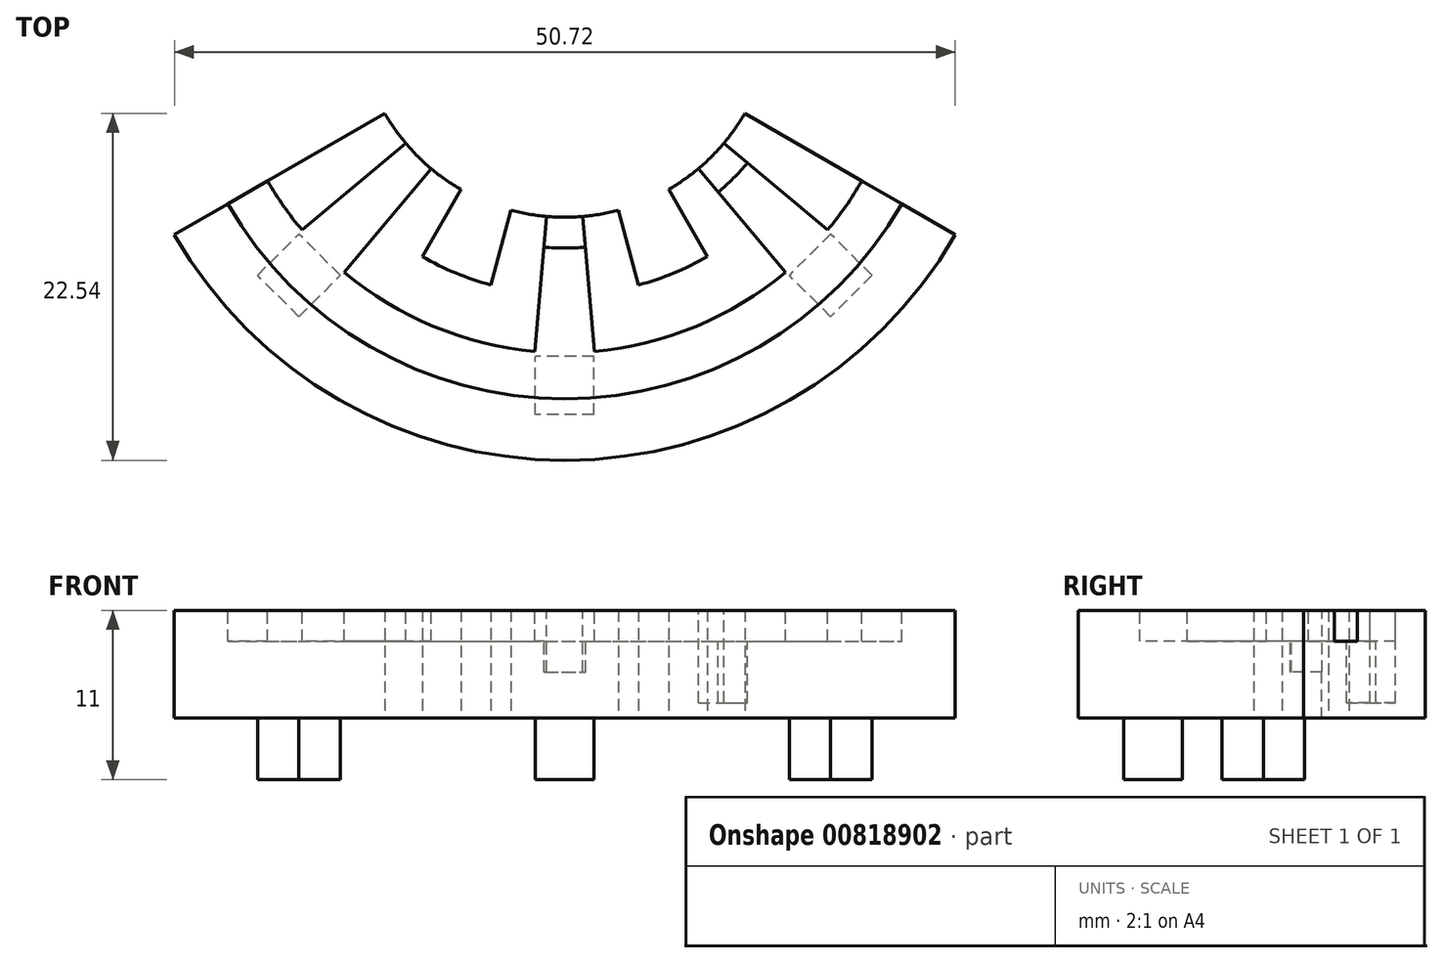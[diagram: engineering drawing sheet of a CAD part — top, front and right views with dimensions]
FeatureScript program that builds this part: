
annotation { "Feature Type Name" : "Feature", "Feature Type Description" : "" }
export const myFeature = defineFeature(function(context is Context, id is Id, definition is map)
    precondition{}
    {
        {
            var Q0;
            Q0=qCreatedBy(makeId("Top.planeOp"),FACE);
            var sketch = newSketch(context, id + "F0", { "sketchPlane" : qUnion([Q0])});
            skCircle(sketch, "E0", {"center": v(0, 0) * mm, "radius": 29.29 * mm});
            skCircle(sketch, "E1.4.0", {"center": v(0, -24.43) * mm, "radius": 1 * mm});
            skCircle(sketch, "E2", {"center": v(0, 0) * mm, "radius": 12.5 * mm});
            skLineSegment(sketch, "E3.bottom", {"start": v(1.9, -26.33) * mm, "end": v(-1.9, -26.33) * mm});
            skLineSegment(sketch, "E3.top", {"start": v(1.9, -22.53) * mm, "end": v(-1.9, -22.53) * mm});
            skLineSegment(sketch, "E3.left", {"start": v(1.9, -26.33) * mm, "end": v(1.9, -22.53) * mm});
            skLineSegment(sketch, "E3.right", {"start": v(-1.9, -26.33) * mm, "end": v(-1.9, -22.53) * mm});
            skLineSegment(sketch, "E4.1.0", {"start": v(19.96, -17.27) * mm, "end": v(17.27, -19.96) * mm});
            skLineSegment(sketch, "E4.1.1", {"start": v(19.96, -17.27) * mm, "end": v(17.27, -14.58) * mm});
            skLineSegment(sketch, "E4.1.2", {"start": v(17.27, -14.58) * mm, "end": v(14.58, -17.27) * mm});
            skLineSegment(sketch, "E4.1.3", {"start": v(17.27, -19.96) * mm, "end": v(14.58, -17.27) * mm});
            skLineSegment(sketch, "E4.2.0", {"start": v(26.33, 1.9) * mm, "end": v(26.33, -1.9) * mm});
            skLineSegment(sketch, "E4.2.1", {"start": v(26.33, 1.9) * mm, "end": v(22.53, 1.9) * mm});
            skLineSegment(sketch, "E4.2.2", {"start": v(22.53, 1.9) * mm, "end": v(22.53, -1.9) * mm});
            skLineSegment(sketch, "E4.2.3", {"start": v(26.33, -1.9) * mm, "end": v(22.53, -1.9) * mm});
            skLineSegment(sketch, "E4.3.0", {"start": v(17.27, 19.96) * mm, "end": v(19.96, 17.27) * mm});
            skLineSegment(sketch, "E4.3.1", {"start": v(17.27, 19.96) * mm, "end": v(14.58, 17.27) * mm});
            skLineSegment(sketch, "E4.3.2", {"start": v(14.58, 17.27) * mm, "end": v(17.27, 14.58) * mm});
            skLineSegment(sketch, "E4.3.3", {"start": v(19.96, 17.27) * mm, "end": v(17.27, 14.58) * mm});
            skLineSegment(sketch, "E4.4.0", {"start": v(-1.9, 26.33) * mm, "end": v(1.9, 26.33) * mm});
            skLineSegment(sketch, "E4.4.1", {"start": v(-1.9, 26.33) * mm, "end": v(-1.9, 22.53) * mm});
            skLineSegment(sketch, "E4.4.2", {"start": v(-1.9, 22.53) * mm, "end": v(1.9, 22.53) * mm});
            skLineSegment(sketch, "E4.4.3", {"start": v(1.9, 26.33) * mm, "end": v(1.9, 22.53) * mm});
            skLineSegment(sketch, "E4.5.0", {"start": v(-19.96, 17.27) * mm, "end": v(-17.27, 19.96) * mm});
            skLineSegment(sketch, "E4.5.1", {"start": v(-19.96, 17.27) * mm, "end": v(-17.27, 14.58) * mm});
            skLineSegment(sketch, "E4.5.2", {"start": v(-17.27, 14.58) * mm, "end": v(-14.58, 17.27) * mm});
            skLineSegment(sketch, "E4.5.3", {"start": v(-17.27, 19.96) * mm, "end": v(-14.58, 17.27) * mm});
            skLineSegment(sketch, "E4.6.0", {"start": v(-26.33, -1.9) * mm, "end": v(-26.33, 1.9) * mm});
            skLineSegment(sketch, "E4.6.1", {"start": v(-26.33, -1.9) * mm, "end": v(-22.53, -1.9) * mm});
            skLineSegment(sketch, "E4.6.2", {"start": v(-22.53, -1.9) * mm, "end": v(-22.53, 1.9) * mm});
            skLineSegment(sketch, "E4.6.3", {"start": v(-26.33, 1.9) * mm, "end": v(-22.53, 1.9) * mm});
            skLineSegment(sketch, "E4.7.0", {"start": v(-17.27, -19.96) * mm, "end": v(-19.96, -17.27) * mm});
            skLineSegment(sketch, "E4.7.1", {"start": v(-17.27, -19.96) * mm, "end": v(-14.58, -17.27) * mm});
            skLineSegment(sketch, "E4.7.2", {"start": v(-14.58, -17.27) * mm, "end": v(-17.27, -14.58) * mm});
            skLineSegment(sketch, "E4.7.3", {"start": v(-19.96, -17.27) * mm, "end": v(-17.27, -14.58) * mm});
            skLineSegment(sketch, "E5", {"start": v(0, 0) * mm, "end": v(25.36, -14.64) * mm});
            skLineSegment(sketch, "E6", {"start": v(0, 0) * mm, "end": v(-25.36, -14.64) * mm});
            skLineSegment(sketch, "E7", {"start": v(0, 0) * mm, "end": v(14.64, -25.36) * mm});
            skLineSegment(sketch, "E8", {"start": v(0, 0) * mm, "end": v(7.58, -28.29) * mm});
            skLineSegment(sketch, "E9", {"start": v(0, 0) * mm, "end": v(-7.58, -28.29) * mm});
            skLineSegment(sketch, "E10", {"start": v(0, 0) * mm, "end": v(-14.64, -25.36) * mm});
            skCircle(sketch, "E11", {"center": v(0, 0) * mm, "radius": 18.53 * mm});
            skCircle(sketch, "E12.0", {"center": v(0, 0) * mm, "radius": 13.5 * mm});
            skSolve(sketch);
        }
        {
            var Q0;
            Q0=makeQuery(id+"F0.imprint","IMPRINT",FACE,{"disambiguationData":[TD([[makeQuery(id+"F0.imprint","IMPRINT",EDGE,{"derivedFrom":sQuery(id+"F0.wireOp",EDGE,"E4.1.0")}),1.0]])]});
            var Q1;
            Q1=makeQuery(id+"F0.imprint","IMPRINT",FACE,{"disambiguationData":[TD([[makeQuery(id+"F0.imprint","IMPRINT",EDGE,{"derivedFrom":sQuery(id+"F0.wireOp",EDGE,"E4.1.0")}),-1.0]])]});
            var Q2;
            {var subQ0=sQuery(id+"F0.wireOp",EDGE,"E12.0");var subQ1=sQuery(id+"F0.wireOp",EDGE,"E5");var subQ2=makeQuery(id+"F0.imprint","INTERSECT",VERTEX,{"derivedFrom":[subQ1,subQ0]});Q2=makeQuery(id+"F0.imprint","IMPRINT",FACE,{"disambiguationData":[TD([[makeQuery(id+"F0.imprint","IMPRINT",EDGE,{"disambiguationData":[TD([[subQ2,-1.0]])],"derivedFrom":subQ1}),-1.0]])]});}
            var Q3;
            {var subQ0=sQuery(id+"F0.wireOp",EDGE,"E7");var subQ1=sQuery(id+"F0.wireOp",EDGE,"E0");var subQ2=makeQuery(id+"F0.imprint","INTERSECT",VERTEX,{"derivedFrom":[subQ1,subQ0]});Q3=makeQuery(id+"F0.imprint","IMPRINT",FACE,{"disambiguationData":[TD([[makeQuery(id+"F0.imprint","IMPRINT",EDGE,{"disambiguationData":[TD([[subQ2,1.0]])],"derivedFrom":subQ1}),1.0]])]});}
            var Q4;
            Q4=makeQuery(id+"F0.imprint","IMPRINT",FACE,{"disambiguationData":[TD([[makeQuery(id+"F0.imprint","IMPRINT",EDGE,{"derivedFrom":sQuery(id+"F0.wireOp",EDGE,"E3.bottom")}),1.0]])]});
            var Q5;
            Q5=makeQuery(id+"F0.imprint","IMPRINT",FACE,{"disambiguationData":[TD([[makeQuery(id+"F0.imprint","IMPRINT",EDGE,{"derivedFrom":sQuery(id+"F0.wireOp",EDGE,"E1.4.0")}),-1.0]])]});
            var Q6;
            Q6=makeQuery(id+"F0.imprint","IMPRINT",FACE,{"disambiguationData":[TD([[makeQuery(id+"F0.imprint","IMPRINT",EDGE,{"derivedFrom":sQuery(id+"F0.wireOp",EDGE,"E1.4.0")}),1.0]])]});
            var Q7;
            {var subQ0=sQuery(id+"F0.wireOp",EDGE,"E12.0");var subQ1=sQuery(id+"F0.wireOp",EDGE,"E8");var subQ2=makeQuery(id+"F0.imprint","INTERSECT",VERTEX,{"derivedFrom":[subQ1,subQ0]});Q7=makeQuery(id+"F0.imprint","IMPRINT",FACE,{"disambiguationData":[TD([[makeQuery(id+"F0.imprint","IMPRINT",EDGE,{"disambiguationData":[TD([[subQ2,-1.0]])],"derivedFrom":subQ1}),-1.0]])]});}
            var Q8;
            {var subQ0=sQuery(id+"F0.wireOp",EDGE,"E9");var subQ1=sQuery(id+"F0.wireOp",EDGE,"E0");var subQ2=makeQuery(id+"F0.imprint","INTERSECT",VERTEX,{"derivedFrom":[subQ1,subQ0]});Q8=makeQuery(id+"F0.imprint","IMPRINT",FACE,{"disambiguationData":[TD([[makeQuery(id+"F0.imprint","IMPRINT",EDGE,{"disambiguationData":[TD([[subQ2,1.0]])],"derivedFrom":subQ1}),1.0]])]});}
            var Q9;
            Q9=makeQuery(id+"F0.imprint","IMPRINT",FACE,{"disambiguationData":[TD([[makeQuery(id+"F0.imprint","IMPRINT",EDGE,{"derivedFrom":sQuery(id+"F0.wireOp",EDGE,"E4.7.0")}),1.0]])]});
            var Q10;
            Q10=makeQuery(id+"F0.imprint","IMPRINT",FACE,{"disambiguationData":[TD([[makeQuery(id+"F0.imprint","IMPRINT",EDGE,{"derivedFrom":sQuery(id+"F0.wireOp",EDGE,"E4.7.0")}),-1.0]])]});
            var Q11;
            {var subQ0=sQuery(id+"F0.wireOp",EDGE,"E12.0");var subQ1=sQuery(id+"F0.wireOp",EDGE,"E6");var subQ2=makeQuery(id+"F0.imprint","INTERSECT",VERTEX,{"derivedFrom":[subQ1,subQ0]});Q11=makeQuery(id+"F0.imprint","IMPRINT",FACE,{"disambiguationData":[TD([[makeQuery(id+"F0.imprint","IMPRINT",EDGE,{"disambiguationData":[TD([[subQ2,-1.0]])],"derivedFrom":subQ1}),1.0]])]});}
            extrude(context, id + "F1", {"entities" : qUnion([Q0, Q1, Q2, Q3, Q4, Q5, Q6, Q7, Q8, Q9, Q10, Q11]), "depth" : 7 * mm, "offsetDistance" : 25 * mm});
        }
        {
            var Q0;
            Q0=makeQuery(id+"F0.imprint","IMPRINT",FACE,{"disambiguationData":[TD([[makeQuery(id+"F0.imprint","IMPRINT",EDGE,{"derivedFrom":sQuery(id+"F0.wireOp",EDGE,"E4.1.0")}),-1.0]])]});
            var Q1;
            Q1=makeQuery(id+"F0.imprint","IMPRINT",FACE,{"disambiguationData":[TD([[makeQuery(id+"F0.imprint","IMPRINT",EDGE,{"derivedFrom":sQuery(id+"F0.wireOp",EDGE,"E1.4.0")}),-1.0]])]});
            var Q2;
            Q2=makeQuery(id+"F0.imprint","IMPRINT",FACE,{"disambiguationData":[TD([[makeQuery(id+"F0.imprint","IMPRINT",EDGE,{"derivedFrom":sQuery(id+"F0.wireOp",EDGE,"E1.4.0")}),1.0]])]});
            var Q3;
            Q3=makeQuery(id+"F0.imprint","IMPRINT",FACE,{"disambiguationData":[TD([[makeQuery(id+"F0.imprint","IMPRINT",EDGE,{"derivedFrom":sQuery(id+"F0.wireOp",EDGE,"E4.7.0")}),-1.0]])]});
            extrude(context, id + "F2", {"entities" : qUnion([Q0, Q1, Q2, Q3]), "operationType" : NewBodyOperationType.ADD, "oppositeDirection" : true, "depth" : 4 * mm, "offsetDistance" : 25 * mm});
        }
        {
            var Q0;
            Q0=qCreatedBy(makeId("Top.planeOp"),FACE);
            cPlane(context, id + "F3", {"entities" : qUnion([Q0]), "cplaneType" : CPlaneType.OFFSET, "offset" : 7 * mm, "width" : 150 * mm, "height" : 150 * mm});
        }
        {
            var Q0;
            Q0=qCreatedBy(id+"F3.planeOp",FACE);
            var sketch = newSketch(context, id + "F4", { "sketchPlane" : qUnion([Q0])});
            skArc(sketch, "E13.0", {"start": v(-25.36, -14.64) * mm, "mid": v(0, -29.29) * mm, "end": v(25.36, -14.64) * mm});
            skLineSegment(sketch, "E14.0", {"start": v(-11.7, -6.75) * mm, "end": v(-25.36, -14.64) * mm});
            skLineSegment(sketch, "E15.0", {"start": v(11.7, -6.75) * mm, "end": v(25.36, -14.64) * mm});
            skCircle(sketch, "E16", {"center": v(0, 0) * mm, "radius": 25.29 * mm});
            skCircle(sketch, "E17", {"center": v(0, 0) * mm, "radius": 22.29 * mm});
            skLineSegment(sketch, "E18", {"start": v(0, 0) * mm, "end": v(-17.07, -14.33) * mm});
            skLineSegment(sketch, "E19", {"start": v(0, 0) * mm, "end": v(-14.33, -17.07) * mm});
            skLineSegment(sketch, "E20", {"start": v(0, 0) * mm, "end": v(-1.94, -22.2) * mm});
            skLineSegment(sketch, "E21", {"start": v(0, 0) * mm, "end": v(1.94, -22.2) * mm});
            skLineSegment(sketch, "E22", {"start": v(0, 0) * mm, "end": v(14.33, -17.07) * mm});
            skLineSegment(sketch, "E23", {"start": v(0, 0) * mm, "end": v(17.07, -14.33) * mm});
            skArc(sketch, "E24.0", {"start": v(-11.7, -6.75) * mm, "mid": v(-9.55, -9.55) * mm, "end": v(-6.75, -11.7) * mm});
            skArc(sketch, "E25.0", {"start": v(-3.5, -13.04) * mm, "mid": v(0, -13.5) * mm, "end": v(3.5, -13.04) * mm});
            skArc(sketch, "E26.0", {"start": v(6.75, -11.7) * mm, "mid": v(9.55, -9.55) * mm, "end": v(11.7, -6.75) * mm});
            skCircle(sketch, "E27", {"center": v(0, 0) * mm, "radius": 15.5 * mm});
            skSolve(sketch);
        }
        {
            var Q0;
            {var subQ0=sQuery(id+"F4.wireOp",EDGE,"E18");var subQ1=sQuery(id+"F4.wireOp",EDGE,"E17");var subQ2=makeQuery(id+"F4.imprint","INTERSECT",VERTEX,{"derivedFrom":[subQ1,subQ0]});Q0=makeQuery(id+"F4.imprint","IMPRINT",FACE,{"disambiguationData":[TD([[makeQuery(id+"F4.imprint","IMPRINT",EDGE,{"disambiguationData":[TD([[subQ2,-1.0]])],"derivedFrom":subQ1}),1.0]])]});}
            var Q1;
            {var subQ0=sQuery(id+"F4.wireOp",EDGE,"E20");var subQ1=sQuery(id+"F4.wireOp",EDGE,"E17");var subQ2=makeQuery(id+"F4.imprint","INTERSECT",VERTEX,{"derivedFrom":[subQ1,subQ0]});Q1=makeQuery(id+"F4.imprint","IMPRINT",FACE,{"disambiguationData":[TD([[makeQuery(id+"F4.imprint","IMPRINT",EDGE,{"disambiguationData":[TD([[subQ2,-1.0]])],"derivedFrom":subQ1}),1.0]])]});}
            var Q2;
            {var subQ0=sQuery(id+"F4.wireOp",EDGE,"E22");var subQ1=sQuery(id+"F4.wireOp",EDGE,"E17");var subQ2=makeQuery(id+"F4.imprint","INTERSECT",VERTEX,{"derivedFrom":[subQ1,subQ0]});Q2=makeQuery(id+"F4.imprint","IMPRINT",FACE,{"disambiguationData":[TD([[makeQuery(id+"F4.imprint","IMPRINT",EDGE,{"disambiguationData":[TD([[subQ2,-1.0]])],"derivedFrom":subQ1}),1.0]])]});}
            var Q3;
            {var subQ2=sQuery(id+"F4.wireOp",EDGE,"E14.0");var subQ4=sQuery(id+"F4.wireOp",EDGE,"E16");var subQ8=makeQuery(id+"F4.imprint","INTERSECT",VERTEX,{"derivedFrom":[subQ2,subQ4]});Q3=makeQuery(id+"F4.imprint","IMPRINT",FACE,{"disambiguationData":[TD([[makeQuery(id+"F4.imprint","IMPRINT",EDGE,{"disambiguationData":[TD([[subQ8,1.0]])],"derivedFrom":subQ2}),1.0]])]});}
            extrude(context, id + "F5", {"entities" : qUnion([Q0, Q1, Q2, Q3]), "operationType" : NewBodyOperationType.REMOVE, "oppositeDirection" : true, "depth" : 2 * mm, "offsetDistance" : 25 * mm});
        }
        {
            var Q0;
            {var subQ0=sQuery(id+"F4.wireOp",EDGE,"E24.0");var subQ1=sQuery(id+"F4.wireOp",EDGE,"E18");var subQ2=makeQuery(id+"F4.imprint","INTERSECT",VERTEX,{"derivedFrom":[subQ1,subQ0]});Q0=makeQuery(id+"F4.imprint","IMPRINT",FACE,{"disambiguationData":[TD([[makeQuery(id+"F4.imprint","IMPRINT",EDGE,{"disambiguationData":[TD([[subQ2,-1.0]])],"derivedFrom":subQ1}),1.0]])]});}
            extrude(context, id + "F6", {"entities" : qUnion([Q0]), "operationType" : NewBodyOperationType.REMOVE, "oppositeDirection" : true, "depth" : 2 * mm, "offsetDistance" : 25 * mm});
        }
        {
            var Q0;
            {var subQ0=sQuery(id+"F4.wireOp",EDGE,"E25.0");var subQ1=sQuery(id+"F4.wireOp",EDGE,"E20");var subQ2=makeQuery(id+"F4.imprint","INTERSECT",VERTEX,{"derivedFrom":[subQ1,subQ0]});Q0=makeQuery(id+"F4.imprint","IMPRINT",FACE,{"disambiguationData":[TD([[makeQuery(id+"F4.imprint","IMPRINT",EDGE,{"disambiguationData":[TD([[subQ2,-1.0]])],"derivedFrom":subQ1}),1.0]])]});}
            extrude(context, id + "F7", {"entities" : qUnion([Q0]), "operationType" : NewBodyOperationType.REMOVE, "oppositeDirection" : true, "depth" : 4 * mm, "offsetDistance" : 25 * mm});
        }
        {
            var Q0;
            {var subQ0=sQuery(id+"F4.wireOp",EDGE,"E26.0");var subQ1=sQuery(id+"F4.wireOp",EDGE,"E22");var subQ2=makeQuery(id+"F4.imprint","INTERSECT",VERTEX,{"derivedFrom":[subQ1,subQ0]});Q0=makeQuery(id+"F4.imprint","IMPRINT",FACE,{"disambiguationData":[TD([[makeQuery(id+"F4.imprint","IMPRINT",EDGE,{"disambiguationData":[TD([[subQ2,-1.0]])],"derivedFrom":subQ1}),1.0]])]});}
            extrude(context, id + "F8", {"entities" : qUnion([Q0]), "operationType" : NewBodyOperationType.REMOVE, "oppositeDirection" : true, "depth" : 6 * mm, "offsetDistance" : 25 * mm});
        }
    });
